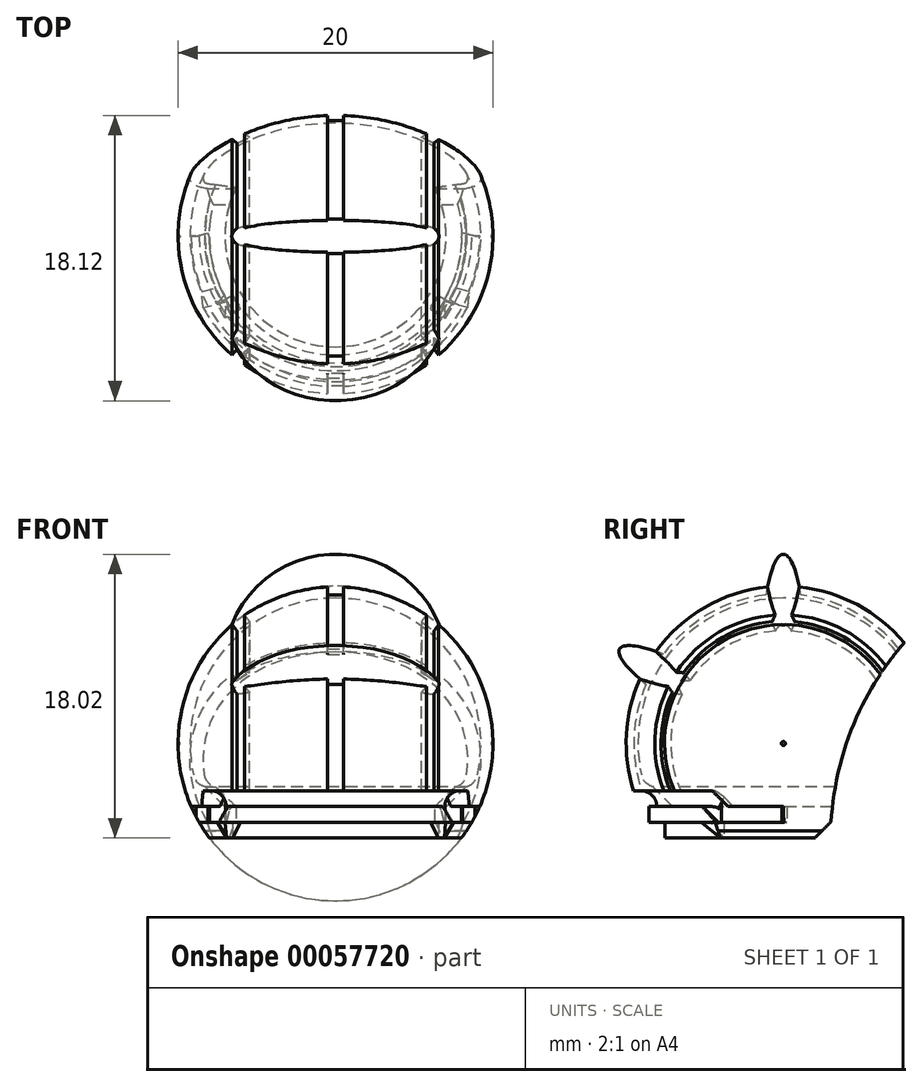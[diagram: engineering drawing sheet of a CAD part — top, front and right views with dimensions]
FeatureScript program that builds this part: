
annotation { "Feature Type Name" : "Feature", "Feature Type Description" : "" }
export const myFeature = defineFeature(function(context is Context, id is Id, definition is map)
    precondition{}
    {
        {
            var Q0;
            Q0=qCreatedBy(makeId("Top.planeOp"),FACE);
            var sketch = newSketch(context, id + "F0", { "sketchPlane" : qUnion([Q0])});
            skArc(sketch, "E0", {"start": v(-10, -0.12) * mm, "mid": v(-9.07, -4.2) * mm, "end": v(-6.56, -7.55) * mm});
            skLineSegment(sketch, "E1", {"start": v(-0.5, -9.99) * mm, "end": v(-0.5, -9.5) * mm});
            skLineSegment(sketch, "E2", {"start": v(-0.5, -9.5) * mm, "end": v(0.5, -9.5) * mm});
            skLineSegment(sketch, "E3", {"start": v(0.5, -9.5) * mm, "end": v(0.5, -9.99) * mm});
            skLineSegment(sketch, "E4", {"start": v(-10, 0) * mm, "end": v(-6.56, -7.55) * mm});
            skLineSegment(sketch, "E5", {"start": v(-6.56, -7.55) * mm, "end": v(-6.25, -7.16) * mm});
            skLineSegment(sketch, "E6", {"start": v(-6.25, -7.16) * mm, "end": v(-5.46, -7.77) * mm});
            skLineSegment(sketch, "E7", {"start": v(-5.46, -7.77) * mm, "end": v(-5.77, -8.17) * mm});
            skLineSegment(sketch, "E8.MirrorCS", {"start": v(5.46, -7.77) * mm, "end": v(5.77, -8.17) * mm});
            skLineSegment(sketch, "E9.MirrorCS", {"start": v(6.25, -7.16) * mm, "end": v(5.46, -7.77) * mm});
            skLineSegment(sketch, "E10.MirrorCS", {"start": v(6.56, -7.55) * mm, "end": v(6.25, -7.16) * mm});
            skArc(sketch, "E11", {"start": v(-10, -0.12) * mm, "mid": v(-9.91, -0.09) * mm, "end": v(-9.88, 0) * mm});
            skLineSegment(sketch, "E12", {"start": v(-9.88, 0) * mm, "end": v(9.88, 0) * mm});
            skArc(sketch, "E13.MirrorCS", {"start": v(10, -0.12) * mm, "mid": v(9.91, -0.09) * mm, "end": v(9.88, 0) * mm});
            skPoint(sketch, "E14.orphan", {"position": v(-10, 0.12) * mm});
            skPoint(sketch, "E15.orphan", {"position": v(10, 0.12) * mm});
            skArc(sketch, "E16.trimOffspring", {"start": v(6.56, -7.55) * mm, "mid": v(9.07, -4.2) * mm, "end": v(10, -0.12) * mm});
            skArc(sketch, "E17.trimOffspring", {"start": v(0.5, -9.99) * mm, "mid": v(3.26, -9.45) * mm, "end": v(5.77, -8.17) * mm});
            skArc(sketch, "E18.trimOffspring", {"start": v(-5.77, -8.17) * mm, "mid": v(-3.26, -9.45) * mm, "end": v(-0.5, -9.99) * mm});
            skSolve(sketch);
        }
        {
            var Q0;
            Q0=makeQuery(id+"F0.imprint","IMPRINT",FACE,{"disambiguationData":[TD([[makeQuery(id+"F0.imprint","IMPRINT",EDGE,{"derivedFrom":sQuery(id+"F0.wireOp",EDGE,"E1")}),1.0]])]});
            var Q1;
            {var subQ0=sQuery(id+"F0.wireOp",EDGE,"E0");Q1=makeQuery(id+"F0.imprint","IMPRINT",FACE,{"disambiguationData":[TD([[makeQuery(id+"F0.imprint","IMPRINT",EDGE,{"derivedFrom":subQ0}),1.0]])]});}
            var Q2;
            Q2=sQuery(id+"F0.wireOp",EDGE,"E12");
            revolve(context, id + "F1", {"entities" : qUnion([Q0, Q1]), "axis" : qUnion([Q2]), "revolveType" : RevolveType.FULL});
        }
        {
            var Q0;
            Q0=qCreatedBy(makeId("Front.planeOp"),FACE);
            var sketch = newSketch(context, id + "F2", { "sketchPlane" : qUnion([Q0])});
            skCircle(sketch, "E19", {"center": v(0, 0) * mm, "radius": 10 * mm});
            skLineSegment(sketch, "E20", {"start": v(0, 10) * mm, "end": v(0, 12) * mm});
            skPoint(sketch, "E21.first.point", {"position": v(6.56, 7.55) * mm});
            skPoint(sketch, "E21.third.point", {"position": v(-6.56, 7.55) * mm});
            skCircle(sketch, "E22", {"center": v(0, 4.95) * mm, "radius": 7.05 * mm});
            skLineSegment(sketch, "E23", {"start": v(0, 4.95) * mm, "end": v(0, 12) * mm});
            skSolve(sketch);
        }
        {
            var Q0;
            Q0=qCreatedBy(makeId("Right.planeOp"),FACE);
            var sketch = newSketch(context, id + "F3", { "sketchPlane" : qUnion([Q0])});
            skLineSegment(sketch, "E24", {"start": v(0, 10) * mm, "end": v(-1, 10) * mm});
            skPoint(sketch, "E25.third.point", {"position": v(0, 12.02) * mm});
            skEllipticalArc(sketch, "E26", {});
            skLineSegment(sketch, "E27", {"start": v(0, 4.95) * mm, "end": v(-1.63, 4.95) * mm});
            skPoint(sketch, "E27.endSnap0", {"position": v(-1.43, 4.95) * mm});
            skLineSegment(sketch, "E28", {"start": v(-1.63, 4.95) * mm, "end": v(1.7, 4.95) * mm});
            const initialGuessF3  = {"E26": [0, 0.004945506933414916, 0, 1, 0.007079370659506341, 0.0014289592947863377, 4.71238898038469, 1.5707963267948966]};
            skSetInitialGuess(sketch, initialGuessF3);
            skSolve(sketch);
        }
        {
            var Q0;
            {var subQ0=sQuery(id+"F3.wireOp",EDGE,"E26");var subQ1=makeQuery(id+"F3.imprint","IMPRINT",VERTEX,{"derivedFrom":subQ0});Q0=makeQuery(id+"F3.imprint","IMPRINT",FACE,{"disambiguationData":[TD([[makeQuery(id+"F3.imprint","IMPRINT",EDGE,{"disambiguationData":[TD([[subQ1,-1.0]])],"derivedFrom":subQ0}),1.0]])]});}
            var Q1;
            Q1=sQuery(id+"F3.wireOp",EDGE,"E28");
            revolve(context, id + "F4", {"operationType" : NewBodyOperationType.ADD, "entities" : qUnion([Q0]), "axis" : qUnion([Q1]), "revolveType" : RevolveType.FULL});
        }
        {
            var Q0;
            Q0=makeQuery(id+"F1.opRevolve","SWEPT_BODY",BODY,{"disambiguationData":[OSD([sQuery(id+"F0.wireOp",EDGE,"E0"),sQuery(id+"F0.wireOp",EDGE,"E1"),sQuery(id+"F0.wireOp",EDGE,"E2"),sQuery(id+"F0.wireOp",EDGE,"E3"),sQuery(id+"F0.wireOp",EDGE,"E5"),sQuery(id+"F0.wireOp",EDGE,"E6"),sQuery(id+"F0.wireOp",EDGE,"E7"),sQuery(id+"F0.wireOp",EDGE,"E8.MirrorCS"),sQuery(id+"F0.wireOp",EDGE,"E9.MirrorCS"),sQuery(id+"F0.wireOp",EDGE,"E10.MirrorCS"),sQuery(id+"F0.wireOp",EDGE,"E11"),sQuery(id+"F0.wireOp",EDGE,"E12"),sQuery(id+"F0.wireOp",EDGE,"E13.MirrorCS"),sQuery(id+"F0.wireOp",EDGE,"E16.trimOffspring"),sQuery(id+"F0.wireOp",EDGE,"E17.trimOffspring"),sQuery(id+"F0.wireOp",EDGE,"E18.trimOffspring")])]});
            var Q1;
            Q1=sQuery(id+"F0.wireOp",EDGE,"E12");
            circularPattern(context, id + "F5", {"operationType" : NewBodyOperationType.ADD, "entities" : qUnion([Q0]), "axis" : qUnion([Q1]), "angle" : 60 * degree, "instanceCount" : 2});
        }
        {
            var Q0;
            Q0=qCreatedBy(makeId("Right.planeOp"),FACE);
            var sketch = newSketch(context, id + "F6", { "sketchPlane" : qUnion([Q0])});
            skLineSegment(sketch, "E29", {"start": v(0, 0) * mm, "end": v(0, -6) * mm});
            skLineSegment(sketch, "E30", {"start": v(-4, -6) * mm, "end": v(2, -6) * mm});
            skLineSegment(sketch, "E31", {"start": v(0, 0) * mm, "end": v(-4, 0) * mm});
            skLineSegment(sketch, "E32", {"start": v(0, 6.2) * mm, "end": v(-7.5, 6.2) * mm});
            skLineSegment(sketch, "E33", {"start": v(11.18, -21.72) * mm, "end": v(9.54, -25.56) * mm});
            skLineSegment(sketch, "E34", {"start": v(9.54, -25.56) * mm, "end": v(-12.52, -21.47) * mm});
            skArc(sketch, "E35.MirrorC", {"start": v(3.03, -4.97) * mm, "mid": v(39.13, 2.23) * mm, "end": v(11.18, -21.72) * mm});
            skLineSegment(sketch, "E36.MirrorCS", {"start": v(4, -6) * mm, "end": v(-15.23, -6) * mm});
            skLineSegment(sketch, "E37.MirrorCS", {"start": v(-15.23, -12.24) * mm, "end": v(-9.54, -25.56) * mm});
            skLineSegment(sketch, "E38.MirrorCS", {"start": v(-15.23, -6) * mm, "end": v(-15.23, -12.24) * mm});
            skLineSegment(sketch, "E39", {"start": v(2, -6) * mm, "end": v(3.03, -4.97) * mm});
            skLineSegment(sketch, "E40.trimOffspring", {"start": v(3, -6) * mm, "end": v(4, -6) * mm});
            skPoint(sketch, "E41.end.orphan", {"position": v(15.23, -12.24) * mm});
            skPoint(sketch, "E41.start.orphan", {"position": v(15.23, -6) * mm});
            skSolve(sketch);
        }
        {
            var Q0;
            {var subQ5=sQuery(id+"F6.wireOp",EDGE,"E33");Q0=makeQuery(id+"F6.imprint","IMPRINT",FACE,{"disambiguationData":[TD([[makeQuery(id+"F6.imprint","IMPRINT",EDGE,{"derivedFrom":subQ5}),-1.0]])]});}
            extrude(context, id + "F7", {"entities" : qUnion([Q0]), "operationType" : NewBodyOperationType.REMOVE, "endBound" : BoundingType.THROUGH_ALL, "oppositeDirection" : true, "depth" : 25 * mm, "hasSecondDirection" : true, "secondDirectionBound" : SecondDirectionBoundingType.THROUGH_ALL, "secondDirectionOppositeDirection" : false, "secondDirectionDepth" : 25 * mm});
        }
        {
            var Q0;
            Q0=qCreatedBy(makeId("Right.planeOp"),FACE);
            var sketch = newSketch(context, id + "F8", { "sketchPlane" : qUnion([Q0])});
            skLineSegment(sketch, "E42", {"start": v(0, -6) * mm, "end": v(-8, -6) * mm});
            skLineSegment(sketch, "E43", {"start": v(0, 0) * mm, "end": v(-8, -6) * mm});
            skLineSegment(sketch, "E44.0", {"start": v(0, -1) * mm, "end": v(-8, -1) * mm});
            skLineSegment(sketch, "E45", {"start": v(-9.54, -3) * mm, "end": v(-8.04, -3) * mm});
            skLineSegment(sketch, "E46", {"start": v(-8.04, -3) * mm, "end": v(-8.04, -4) * mm});
            skLineSegment(sketch, "E47", {"start": v(-8.04, -4) * mm, "end": v(-8.54, -4) * mm});
            skLineSegment(sketch, "E48", {"start": v(-8.54, -4) * mm, "end": v(-8.54, -5) * mm});
            skLineSegment(sketch, "E49", {"start": v(-8.54, -5) * mm, "end": v(-7.54, -5) * mm});
            skLineSegment(sketch, "E50", {"start": v(-7.54, -5) * mm, "end": v(-7.54, -6) * mm});
            skLineSegment(sketch, "E51", {"start": v(0, 0) * mm, "end": v(-9.54, -3) * mm});
            skLineSegment(sketch, "E52", {"start": v(-9.54, -3) * mm, "end": v(-9.54, -6.02) * mm});
            skLineSegment(sketch, "E53", {"start": v(-9.54, -6.02) * mm, "end": v(-8, -6) * mm});
            skLineSegment(sketch, "E54", {"start": v(-8.04, -3) * mm, "end": v(-6.02, -3) * mm});
            skLineSegment(sketch, "E55", {"start": v(-6.02, -3) * mm, "end": v(-6.02, -6) * mm});
            skLineSegment(sketch, "E56", {"start": v(-8.54, -4) * mm, "end": v(-9.54, -4) * mm});
            skLineSegment(sketch, "E57", {"start": v(-8.54, -5) * mm, "end": v(-9.54, -5) * mm});
            skSolve(sketch);
        }
        {
            var Q0;
            Q0=makeQuery(id+"F8.imprint","IMPRINT",FACE,{"disambiguationData":[TD([[makeQuery(id+"F8.imprint","IMPRINT",EDGE,{"derivedFrom":sQuery(id+"F8.wireOp",EDGE,"E45")}),-1.0]])]});
            var Q1;
            {var subQ1=sQuery(id+"F8.wireOp",EDGE,"E42");var subQ3=sQuery(id+"F8.wireOp",EDGE,"E50");var subQ4=makeQuery(id+"F8.imprint","INTERSECT",VERTEX,{"derivedFrom":[subQ1,subQ3]});Q1=makeQuery(id+"F8.imprint","IMPRINT",FACE,{"disambiguationData":[TD([[makeQuery(id+"F8.imprint","IMPRINT",EDGE,{"disambiguationData":[TD([[subQ4,1.0]])],"derivedFrom":subQ3}),-1.0]])]});}
            var Q2;
            Q2=makeQuery(id+"F8.imprint","IMPRINT",FACE,{"disambiguationData":[TD([[makeQuery(id+"F8.imprint","IMPRINT",EDGE,{"derivedFrom":sQuery(id+"F8.wireOp",EDGE,"E48")}),-1.0]])]});
            var Q3;
            {var subQ0=sQuery(id+"F8.wireOp",EDGE,"E49");Q3=makeQuery(id+"F8.imprint","IMPRINT",FACE,{"disambiguationData":[TD([[makeQuery(id+"F8.imprint","IMPRINT",EDGE,{"derivedFrom":subQ0}),-1.0]])]});}
            var Q4;
            Q4=sQuery(id+"F6.wireOp",EDGE,"E29");
            revolve(context, id + "F9", {"operationType" : NewBodyOperationType.REMOVE, "entities" : qUnion([Q0, Q1, Q2, Q3]), "axis" : qUnion([Q4]), "revolveType" : RevolveType.SYMMETRIC, "oppositeDirection" : true, "angle" : 120 * degree});
        }
        {
            var Q0;
            {var subQ0=sQuery(id+"F8.wireOp",EDGE,"E50");var subQ1=sQuery(id+"F8.wireOp",EDGE,"E42");var subQ2=makeQuery(id+"F8.imprint","INTERSECT",VERTEX,{"derivedFrom":[subQ1,subQ0]});Q0=makeQuery(id+"F8.imprint","IMPRINT",FACE,{"disambiguationData":[TD([[makeQuery(id+"F8.imprint","IMPRINT",EDGE,{"disambiguationData":[TD([[subQ2,1.0]])],"derivedFrom":subQ1}),-1.0]])]});}
            var Q1;
            Q1=makeQuery(id+"F8.imprint","IMPRINT",FACE,{"disambiguationData":[TD([[makeQuery(id+"F8.imprint","IMPRINT",EDGE,{"derivedFrom":sQuery(id+"F8.wireOp",EDGE,"E46")}),1.0]])]});
            var Q2;
            Q2=sQuery(id+"F6.wireOp",EDGE,"E29");
            revolve(context, id + "F10", {"operationType" : NewBodyOperationType.ADD, "entities" : qUnion([Q0, Q1]), "axis" : qUnion([Q2]), "revolveType" : RevolveType.SYMMETRIC, "angle" : 120 * degree});
        }
        {
            var Q0;
            Q0=makeQuery(id+"F8.imprint","IMPRINT",FACE,{"disambiguationData":[TD([[makeQuery(id+"F8.imprint","IMPRINT",EDGE,{"derivedFrom":sQuery(id+"F8.wireOp",EDGE,"E48")}),-1.0]])]});
            var Q1;
            Q1=sQuery(id+"F6.wireOp",EDGE,"E29");
            revolve(context, id + "F11", {"operationType" : NewBodyOperationType.REMOVE, "entities" : qUnion([Q0]), "axis" : qUnion([Q1]), "revolveType" : RevolveType.SYMMETRIC, "angle" : 180 * degree});
        }
        {
            var Q0;
            Q0=makeQuery(id+"F11.boolean.opBoolean","COPY",VERTEX,{"derivedFrom":makeQuery(id+"F11.opRevolve","CAP_VERTEX",VERTEX,{"disambiguationData":[OSD([sQuery(id+"F8.wireOp",EDGE,"E47"),sQuery(id+"F8.wireOp",EDGE,"E48"),sQuery(id+"F8.wireOp",EDGE,"E56")])],"isStart":false})});
            var Q1;
            Q1=makeQuery(id+"F9.boolean.opBoolean","COPY",VERTEX,{"derivedFrom":makeQuery(id+"F9.opRevolve","CAP_VERTEX",VERTEX,{"disambiguationData":[OSD([sQuery(id+"F8.wireOp",EDGE,"E47"),sQuery(id+"F8.wireOp",EDGE,"E48"),sQuery(id+"F8.wireOp",EDGE,"E56")])],"isStart":true})});
            var Q2;
            Q2=makeQuery(id+"F11.boolean.opBoolean","COPY",VERTEX,{"derivedFrom":makeQuery(id+"F11.opRevolve","CAP_VERTEX",VERTEX,{"disambiguationData":[OSD([sQuery(id+"F8.wireOp",EDGE,"E48"),sQuery(id+"F8.wireOp",EDGE,"E49"),sQuery(id+"F8.wireOp",EDGE,"E57")])],"isStart":false})});
            cPlane(context, id + "F12", {"entities" : qUnion([Q0, Q1, Q2]), "cplaneType" : CPlaneType.THREE_POINT, "offset" : 150 * mm, "width" : 150 * mm, "height" : 150 * mm});
        }
        {
            var Q0;
            Q0=qCreatedBy(id+"F12.planeOp",FACE);
            var sketch = newSketch(context, id + "F13", { "sketchPlane" : qUnion([Q0])});
            skLineSegment(sketch, "E58", {"start": v(2.2, -3) * mm, "end": v(1.2, -4) * mm});
            skLineSegment(sketch, "E59", {"start": v(1.2, -4) * mm, "end": v(-2.3, -4) * mm});
            skLineSegment(sketch, "E60", {"start": v(-2.3, -4) * mm, "end": v(-2.3, -5) * mm});
            skLineSegment(sketch, "E61", {"start": v(-2.3, -5) * mm, "end": v(2.2, -5) * mm});
            skLineSegment(sketch, "E62", {"start": v(2.2, -5) * mm, "end": v(3.2, -4) * mm});
            skLineSegment(sketch, "E63", {"start": v(3.2, -4) * mm, "end": v(3.2, -3) * mm});
            skLineSegment(sketch, "E64", {"start": v(3.2, -3) * mm, "end": v(2.2, -3) * mm});
            skLineSegment(sketch, "E65", {"start": v(2.2, -4.93) * mm, "end": v(2.2, -5) * mm});
            skLineSegment(sketch, "E66", {"start": v(-2.3, -5) * mm, "end": v(-2.21, -6.55) * mm});
            skLineSegment(sketch, "E67", {"start": v(-2.21, -6.55) * mm, "end": v(2.22, -6.55) * mm});
            skLineSegment(sketch, "E68", {"start": v(2.22, -6.55) * mm, "end": v(2.53, -4.68) * mm});
            skSolve(sketch);
        }
        {
            var Q0;
            Q0=makeQuery(id+"F13.imprint","IMPRINT",FACE,{"disambiguationData":[TD([[makeQuery(id+"F13.imprint","IMPRINT",EDGE,{"derivedFrom":sQuery(id+"F13.wireOp",EDGE,"E58")}),1.0]])]});
            extrude(context, id + "F14", {"entities" : qUnion([Q0]), "operationType" : NewBodyOperationType.REMOVE, "endBound" : BoundingType.THROUGH_ALL, "depth" : 25 * mm, "hasSecondDirection" : true, "secondDirectionOppositeDirection" : true, "secondDirectionDepth" : .5 * mm});
        }
        {
            var Q0;
            Q0=makeQuery(id+"F14.boolean.opBoolean","INTERSECT",EDGE,{"derivedFrom":[makeQuery(id+"F9.boolean.opBoolean","COPY",FACE,{"derivedFrom":makeQuery(id+"F9.opRevolve","SWEPT_FACE",FACE,{"disambiguationData":[OSD([sQuery(id+"F8.wireOp",EDGE,"E47")])]})}),makeQuery(id+"F14.opExtrude","CAP_FACE",FACE,{"disambiguationData":[OSD([sQuery(id+"F13.wireOp",EDGE,"E58"),sQuery(id+"F13.wireOp",EDGE,"E59"),sQuery(id+"F13.wireOp",EDGE,"E60"),sQuery(id+"F13.wireOp",EDGE,"E61"),sQuery(id+"F13.wireOp",EDGE,"E62"),sQuery(id+"F13.wireOp",EDGE,"E63"),sQuery(id+"F13.wireOp",EDGE,"E64")])],"isStart":true})]});
            var Q1;
            Q1=makeQuery(id+"F14.boolean.opBoolean","INTERSECT",EDGE,{"derivedFrom":[makeQuery(id+"F9.boolean.opBoolean","COPY",FACE,{"derivedFrom":makeQuery(id+"F9.opRevolve","SWEPT_FACE",FACE,{"disambiguationData":[OSD([sQuery(id+"F8.wireOp",EDGE,"E46")])]})}),makeQuery(id+"F14.opExtrude","CAP_FACE",FACE,{"disambiguationData":[OSD([sQuery(id+"F13.wireOp",EDGE,"E58"),sQuery(id+"F13.wireOp",EDGE,"E59"),sQuery(id+"F13.wireOp",EDGE,"E60"),sQuery(id+"F13.wireOp",EDGE,"E61"),sQuery(id+"F13.wireOp",EDGE,"E62"),sQuery(id+"F13.wireOp",EDGE,"E63"),sQuery(id+"F13.wireOp",EDGE,"E64")])],"isStart":true})]});
            fillet(context, id + "F15", {"entities" : qUnion([Q0, Q1]), "radius" : .2 * mm, "tangentPropagation" : true, "allowEdgeOverflow" : false});
        }
        {
            var Q0;
            {var subQ0=sQuery(id+"F8.wireOp",EDGE,"E48");var subQ1=sQuery(id+"F8.wireOp",EDGE,"E50");var subQ2=sQuery(id+"F8.wireOp",EDGE,"E42");var subQ3=sQuery(id+"F8.wireOp",EDGE,"E49");Q0=makeQuery(id+"F11.boolean.opBoolean","SPLIT",FACE,{"disambiguationData":[TD([makeQuery(id+"F7.boolean.opBoolean","COPY",FACE,{"derivedFrom":makeQuery(id+"F7.opExtrude","SWEPT_FACE",FACE,{"disambiguationData":[OSD([sQuery(id+"F6.wireOp",EDGE,"E36.MirrorCS")])]})})])],"derivedFrom":makeQuery(id+"F9.boolean.opBoolean","COPY",FACE,{"derivedFrom":makeQuery(id+"F9.opRevolve","CAP_FACE",FACE,{"disambiguationData":[OSD([subQ2,sQuery(id+"F8.wireOp",EDGE,"E45"),sQuery(id+"F8.wireOp",EDGE,"E46"),sQuery(id+"F8.wireOp",EDGE,"E47"),subQ0,subQ3,subQ1,sQuery(id+"F8.wireOp",EDGE,"E52"),sQuery(id+"F8.wireOp",EDGE,"E53")])],"isStart":true})})});}
            var sketch = newSketch(context, id + "F16", { "sketchPlane" : qUnion([Q0])});
            skLineSegment(sketch, "E69", {"start": v(-8.66, -5) * mm, "end": v(-8, -6) * mm});
            skLineSegment(sketch, "E70", {"start": v(-8, -6) * mm, "end": v(-7.54, -6) * mm});
            skLineSegment(sketch, "E71", {"start": v(-7.54, -6) * mm, "end": v(-7.54, -5) * mm});
            skLineSegment(sketch, "E72", {"start": v(-7.54, -5) * mm, "end": v(-8.66, -5) * mm});
            skSolve(sketch);
        }
        {
            var Q0;
            {var subQ5=sQuery(id+"F16.wireOp",EDGE,"E69");Q0=makeQuery(id+"F16.imprint","IMPRINT",FACE,{"disambiguationData":[TD([[makeQuery(id+"F16.imprint","IMPRINT",EDGE,{"derivedFrom":subQ5}),1.0]])]});}
            extrude(context, id + "F17", {"entities" : qUnion([Q0]), "operationType" : NewBodyOperationType.ADD, "depth" : 1 * mm, "hasSecondDirection" : true, "secondDirectionOppositeDirection" : true, "secondDirectionDepth" : .25 * mm});
        }
        {
            var Q0;
            Q0=makeQuery(id+"F17.opExtrude","CAP_EDGE",EDGE,{"disambiguationData":[OSD([sQuery(id+"F16.wireOp",EDGE,"E70")])],"isStart":false});
            chamfer(context, id + "F18", {"entities" : qUnion([Q0]), "width" : 1 * mm, "tangentPropagation" : true});
        }
        {
            var Q0;
            {var subQ5=sQuery(id+"F6.wireOp",EDGE,"E33");Q0=makeQuery(id+"F6.imprint","IMPRINT",FACE,{"disambiguationData":[TD([[makeQuery(id+"F6.imprint","IMPRINT",EDGE,{"derivedFrom":subQ5}),-1.0]])]});}
            var sketch = newSketch(context, id + "F19", { "sketchPlane" : qUnion([Q0])});
            skArc(sketch, "E73", {"start": v(-8.32, -5.54) * mm, "mid": v(-8.15, -5.8) * mm, "end": v(-7.97, -6.04) * mm});
            skLineSegment(sketch, "E74", {"start": v(-8.32, -5.54) * mm, "end": v(-8.74, -5.56) * mm});
            skLineSegment(sketch, "E75", {"start": v(-8.74, -5.56) * mm, "end": v(-8.72, -6.01) * mm});
            skLineSegment(sketch, "E76", {"start": v(-8.72, -6.01) * mm, "end": v(-7.97, -6.04) * mm});
            skLineSegment(sketch, "E77", {"start": v(0, 0) * mm, "end": v(0, 0.98) * mm});
            skSolve(sketch);
        }
        {
            var Q0;
            {var subQ0=sQuery(id+"F19.wireOp",EDGE,"E74");Q0=makeQuery(id+"F19.imprint","IMPRINT",FACE,{"disambiguationData":[TD([[makeQuery(id+"F19.imprint","IMPRINT",EDGE,{"derivedFrom":subQ0}),1.0]])]});}
            var Q1;
            Q1=sQuery(id+"F19.wireOp",EDGE,"E77");
            revolve(context, id + "F20", {"operationType" : NewBodyOperationType.REMOVE, "entities" : qUnion([Q0]), "axis" : qUnion([Q1]), "revolveType" : RevolveType.FULL});
        }
        {
            var Q0;
            Q0=makeQuery(id+"F17.boolean.opBoolean","MERGE",FACE,{"derivedFrom":[makeQuery(id+"F10.boolean.opBoolean","MERGE",FACE,{"derivedFrom":[makeQuery(id+"F7.boolean.opBoolean","COPY",FACE,{"derivedFrom":makeQuery(id+"F7.opExtrude","SWEPT_FACE",FACE,{"disambiguationData":[OSD([sQuery(id+"F6.wireOp",EDGE,"E36.MirrorCS")])]})}),makeQuery(id+"F10.opRevolve","SWEPT_FACE",FACE,{"disambiguationData":[OSD([sQuery(id+"F8.wireOp",EDGE,"E42")])]})]}),makeQuery(id+"F17.opExtrude","SWEPT_FACE",FACE,{"disambiguationData":[OSD([sQuery(id+"F16.wireOp",EDGE,"E70")])]})]});
            var sketch = newSketch(context, id + "F21", { "sketchPlane" : qUnion([Q0])});
            skLineSegment(sketch, "E78", {"start": v(0, -8.55) * mm, "end": v(0, 12.43) * mm});
            skLineSegment(sketch, "E79", {"start": v(0, 12.43) * mm, "end": v(14.14, 12.43) * mm});
            skLineSegment(sketch, "E80", {"start": v(14.14, 12.43) * mm, "end": v(13.22, -8.17) * mm});
            skLineSegment(sketch, "E81", {"start": v(13.22, -8.17) * mm, "end": v(-0.58, -8.57) * mm});
            skPoint(sketch, "E82.orphan", {"position": v(0, 0) * mm});
            skSolve(sketch);
        }
        {
            var Q0;
            {var subQ0=sQuery(id+"F21.wireOp",EDGE,"E79");Q0=makeQuery(id+"F21.imprint","IMPRINT",FACE,{"disambiguationData":[TD([[makeQuery(id+"F21.imprint","IMPRINT",EDGE,{"derivedFrom":subQ0}),-1.0]])]});}
            var Q1;
            {var subQ5=sQuery(id+"F8.wireOp",EDGE,"E42");var subQ6=makeQuery(id+"F9.boolean.opBoolean","COPY",EDGE,{"derivedFrom":makeQuery(id+"F9.opRevolve","CAP_EDGE",EDGE,{"disambiguationData":[OSD([subQ5])],"isStart":false})});Q1=makeQuery(id+"F21.imprint","IMPRINT",FACE,{"disambiguationData":[TD([[makeQuery(id+"F21.imprint","IMPRINT",EDGE,{"derivedFrom":subQ6}),-1.0]])]});}
            extrude(context, id + "F22", {"entities" : qUnion([Q0, Q1]), "operationType" : NewBodyOperationType.REMOVE, "endBound" : BoundingType.THROUGH_ALL, "oppositeDirection" : true, "depth" : 25 * mm});
        }
        {
            var Q0;
            Q0=makeQuery(id+"F1.opRevolve","SWEPT_BODY",BODY,{"disambiguationData":[OSD([sQuery(id+"F0.wireOp",EDGE,"E0"),sQuery(id+"F0.wireOp",EDGE,"E1"),sQuery(id+"F0.wireOp",EDGE,"E2"),sQuery(id+"F0.wireOp",EDGE,"E3"),sQuery(id+"F0.wireOp",EDGE,"E5"),sQuery(id+"F0.wireOp",EDGE,"E6"),sQuery(id+"F0.wireOp",EDGE,"E7"),sQuery(id+"F0.wireOp",EDGE,"E8.MirrorCS"),sQuery(id+"F0.wireOp",EDGE,"E9.MirrorCS"),sQuery(id+"F0.wireOp",EDGE,"E10.MirrorCS"),sQuery(id+"F0.wireOp",EDGE,"E11"),sQuery(id+"F0.wireOp",EDGE,"E12"),sQuery(id+"F0.wireOp",EDGE,"E13.MirrorCS"),sQuery(id+"F0.wireOp",EDGE,"E16.trimOffspring"),sQuery(id+"F0.wireOp",EDGE,"E17.trimOffspring"),sQuery(id+"F0.wireOp",EDGE,"E18.trimOffspring")])]});
            var Q1;
            Q1=makeQuery(id+"F22.boolean.opBoolean","COPY",FACE,{"derivedFrom":makeQuery(id+"F22.opExtrude","SWEPT_FACE",FACE,{"disambiguationData":[OSD([sQuery(id+"F21.wireOp",EDGE,"E78")])]})});
            mirror(context, id + "F23", {"operationType" : NewBodyOperationType.ADD, "entities" : qUnion([Q0]), "mirrorPlane" : qUnion([Q1])});
        }
        {
            var Q0;
            Q0=qCreatedBy(makeId("Right.planeOp"),FACE);
            var sketch = newSketch(context, id + "F24", { "sketchPlane" : qUnion([Q0])});
            skCircle(sketch, "E83", {"center": v(0, 0) * mm, "radius": 9.24 * mm});
            skLineSegment(sketch, "E84", {"start": v(-8.82, -2.75) * mm, "end": v(-7.02, -2.75) * mm});
            skLineSegment(sketch, "E85", {"start": v(-7.02, -2.75) * mm, "end": v(-7.02, -6) * mm});
            skLineSegment(sketch, "E86", {"start": v(-7.02, -6) * mm, "end": v(0, -6) * mm});
            skLineSegment(sketch, "E87", {"start": v(0, -6) * mm, "end": v(0, 15.92) * mm});
            skSolve(sketch);
        }
        {
            var Q0;
            {var subQ0=sQuery(id+"F24.wireOp",EDGE,"E84");Q0=makeQuery(id+"F24.imprint","IMPRINT",FACE,{"disambiguationData":[TD([[makeQuery(id+"F24.imprint","IMPRINT",EDGE,{"derivedFrom":subQ0}),1.0]])]});}
            var Q1;
            Q1=sQuery(id+"F24.wireOp",EDGE,"E87");
            revolve(context, id + "F25", {"operationType" : NewBodyOperationType.REMOVE, "entities" : qUnion([Q0]), "axis" : qUnion([Q1]), "revolveType" : RevolveType.FULL, "oppositeDirection" : true});
        }
        {
            var Q0;
            Q0=makeQuery(id+"F25.boolean.opBoolean","COPY",EDGE,{"derivedFrom":makeQuery(id+"F25.opRevolve","SWEPT_EDGE",EDGE,{"disambiguationData":[OSD([sQuery(id+"F24.wireOp",EDGE,"E84"),sQuery(id+"F24.wireOp",EDGE,"E85")])]})});
            chamfer(context, id + "F26", {"entities" : qUnion([Q0]), "width" : 1.26 * mm, "tangentPropagation" : true});
        }
        {
            var Q0;
            {var subQ0=makeQuery(id+"F9.boolean.opBoolean","COPY",EDGE,{"derivedFrom":makeQuery(id+"F9.opRevolve","SWEPT_EDGE",EDGE,{"disambiguationData":[OSD([sQuery(id+"F8.wireOp",EDGE,"E45"),sQuery(id+"F8.wireOp",EDGE,"E46"),sQuery(id+"F8.wireOp",EDGE,"E54")])]})});Q0=makeQuery(id+"F23.boolean.opBoolean","MERGE",EDGE,{"derivedFrom":[subQ0,makeQuery(id+"F23.opPattern","COPY",EDGE,{"derivedFrom":subQ0,"instanceName":"1"})]});}
            var Q1;
            Q1=makeQuery(id+"F25.boolean.opBoolean","COPY",EDGE,{"derivedFrom":makeQuery(id+"F25.opRevolve","SWEPT_EDGE",EDGE,{"disambiguationData":[OSD([sQuery(id+"F24.wireOp",EDGE,"E83"),sQuery(id+"F24.wireOp",EDGE,"E84")])]})});
            fillet(context, id + "F27", {"entities" : qUnion([Q0, Q1]), "radius" : 1 * mm, "tangentPropagation" : true, "allowEdgeOverflow" : false});
        }
    });
